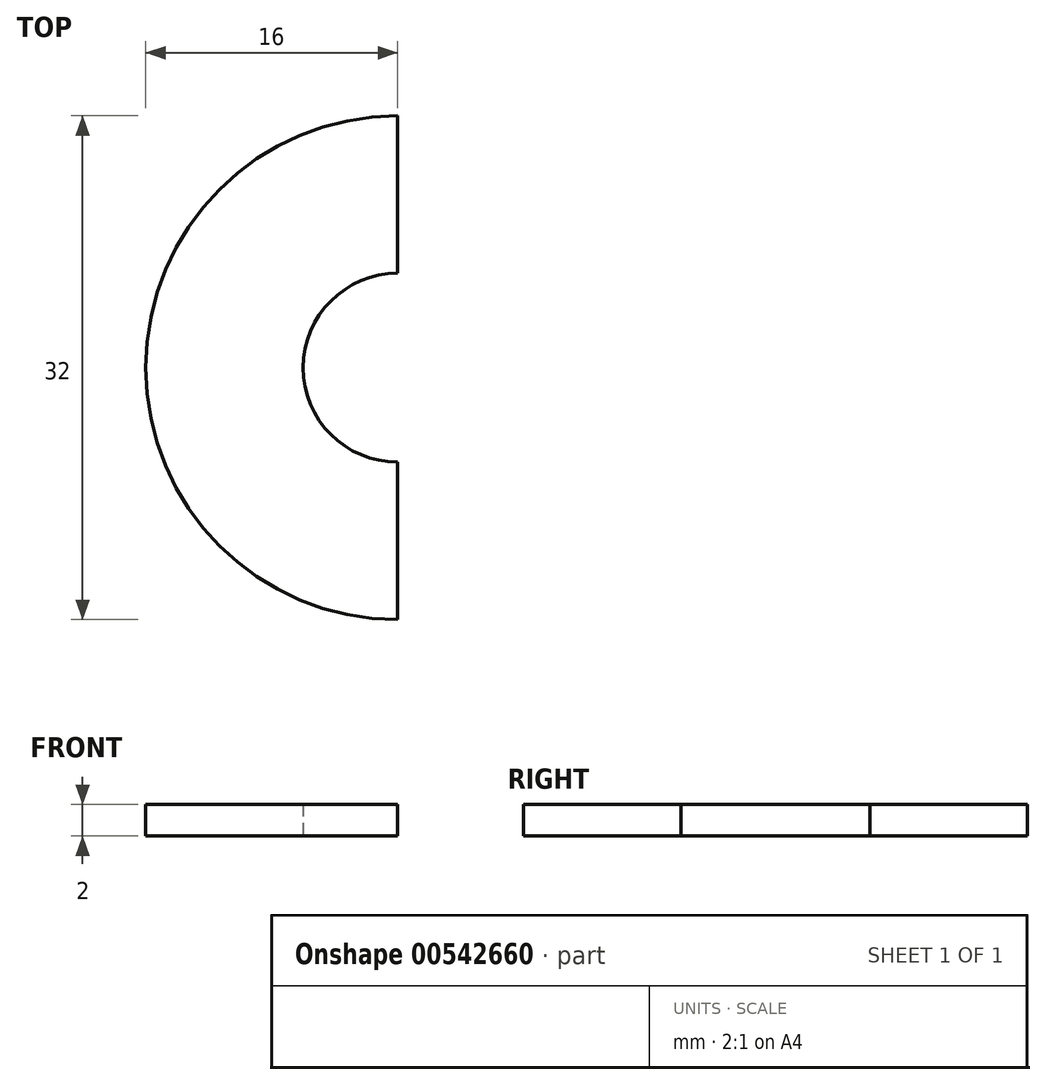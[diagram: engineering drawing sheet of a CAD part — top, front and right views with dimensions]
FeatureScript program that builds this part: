
annotation { "Feature Type Name" : "Feature", "Feature Type Description" : "" }
export const myFeature = defineFeature(function(context is Context, id is Id, definition is map)
    precondition{}
    {
        {
            var Q0;
            Q0=qCreatedBy(makeId("Top.planeOp"),FACE);
            var sketch = newSketch(context, id + "F0", { "sketchPlane" : qUnion([Q0])});
            skCircle(sketch, "E0", {"center": v(0, 0) * mm, "radius": 16 * mm});
            skSolve(sketch);
        }
        {
            var Q0;
            Q0=makeQuery(id+"F0.imprint","IMPRINT",FACE,{"disambiguationData":[TD([[makeQuery(id+"F0.imprint","IMPRINT",EDGE,{"derivedFrom":sQuery(id+"F0.wireOp",EDGE,"E0")}),1.0]])]});
            extrude(context, id + "F1", {"entities" : qUnion([Q0]), "depth" : 2 * mm, "offsetDistance" : 25 * mm});
        }
        {
            var Q0;
            Q0=qCreatedBy(makeId("Top.planeOp"),FACE);
            var sketch = newSketch(context, id + "F2", { "sketchPlane" : qUnion([Q0])});
            skCircle(sketch, "E1", {"center": v(0, 0) * mm, "radius": 6 * mm});
            skSolve(sketch);
        }
        {
            var Q0;
            Q0 = qSketchRegion(id + "F2", true);
            extrude(context, id + "F3", {"entities" : qUnion([Q0]), "operationType" : NewBodyOperationType.REMOVE, "depth" : 25 * mm, "offsetDistance" : 25 * mm});
        }
        {
            var Q0;
            Q0=qCreatedBy(makeId("Top.planeOp"),FACE);
            var sketch = newSketch(context, id + "F4", { "sketchPlane" : qUnion([Q0])});
            skLineSegment(sketch, "E2.bottom", {"start": v(0, 20.82) * mm, "end": v(41.04, 20.82) * mm});
            skLineSegment(sketch, "E2.top", {"start": v(0, -20.6) * mm, "end": v(41.04, -20.6) * mm});
            skLineSegment(sketch, "E2.left", {"start": v(0, 20.82) * mm, "end": v(0, -20.6) * mm});
            skLineSegment(sketch, "E2.right", {"start": v(41.04, 20.82) * mm, "end": v(41.04, -20.6) * mm});
            skSolve(sketch);
        }
        {
            var Q0;
            Q0 = qSketchRegion(id + "F4", true);
            extrude(context, id + "F5", {"entities" : qUnion([Q0]), "operationType" : NewBodyOperationType.REMOVE, "depth" : 25 * mm, "offsetDistance" : 25 * mm});
        }
    });
